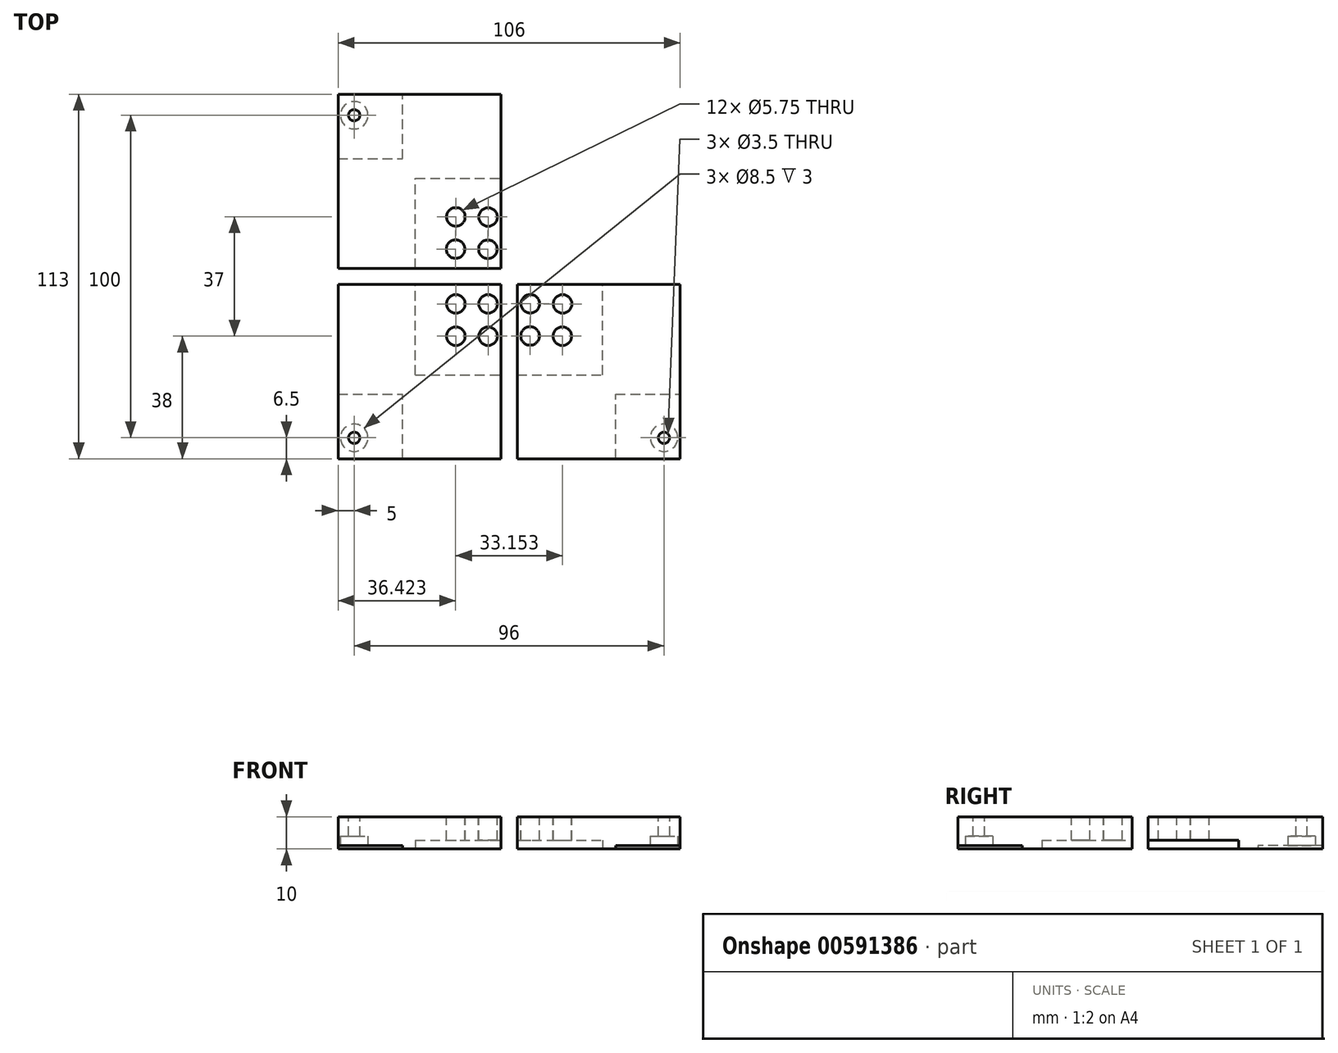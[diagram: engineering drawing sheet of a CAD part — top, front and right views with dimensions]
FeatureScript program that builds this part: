
annotation { "Feature Type Name" : "Feature", "Feature Type Description" : "" }
export const myFeature = defineFeature(function(context is Context, id is Id, definition is map)
    precondition{}
    {
        {
            var Q0;
            Q0=qCreatedBy(makeId("Top.planeOp"),FACE);
            var sketch = newSketch(context, id + "F0", { "sketchPlane" : qUnion([Q0])});
            skLineSegment(sketch, "E0.bottom", {"start": v(-53, 56.5) * mm, "end": v(-2.5, 56.5) * mm});
            skLineSegment(sketch, "E0.top", {"start": v(-53, 2.5) * mm, "end": v(-2.5, 2.5) * mm});
            skLineSegment(sketch, "E0.left", {"start": v(-53, 56.5) * mm, "end": v(-53, 2.5) * mm});
            skLineSegment(sketch, "E0.right", {"start": v(-2.5, 56.5) * mm, "end": v(-2.5, 2.5) * mm});
            skLineSegment(sketch, "E1.bottom", {"start": v(2.5, -2.5) * mm, "end": v(53, -2.5) * mm});
            skLineSegment(sketch, "E1.top", {"start": v(2.5, -56.5) * mm, "end": v(53, -56.5) * mm});
            skLineSegment(sketch, "E1.left", {"start": v(2.5, -2.5) * mm, "end": v(2.5, -56.5) * mm});
            skLineSegment(sketch, "E1.right", {"start": v(53, -2.5) * mm, "end": v(53, -56.5) * mm});
            skLineSegment(sketch, "E2.bottom", {"start": v(-53, -2.5) * mm, "end": v(-2.5, -2.5) * mm});
            skLineSegment(sketch, "E2.top", {"start": v(-53, -56.5) * mm, "end": v(-2.5, -56.5) * mm});
            skLineSegment(sketch, "E2.left", {"start": v(-53, -2.5) * mm, "end": v(-53, -56.5) * mm});
            skLineSegment(sketch, "E2.right", {"start": v(-2.5, -2.5) * mm, "end": v(-2.5, -56.5) * mm});
            skSolve(sketch);
        }
        {
            var Q0;
            Q0=makeQuery(id+"F0.imprint","IMPRINT",FACE,{"disambiguationData":[TD([[makeQuery(id+"F0.imprint","IMPRINT",EDGE,{"derivedFrom":sQuery(id+"F0.wireOp",EDGE,"E0.bottom")}),-1.0]])]});
            var Q1;
            Q1=makeQuery(id+"F0.imprint","IMPRINT",FACE,{"disambiguationData":[TD([[makeQuery(id+"F0.imprint","IMPRINT",EDGE,{"derivedFrom":sQuery(id+"F0.wireOp",EDGE,"E2.bottom")}),-1.0]])]});
            var Q2;
            Q2=makeQuery(id+"F0.imprint","IMPRINT",FACE,{"disambiguationData":[TD([[makeQuery(id+"F0.imprint","IMPRINT",EDGE,{"derivedFrom":sQuery(id+"F0.wireOp",EDGE,"E1.bottom")}),-1.0]])]});
            extrude(context, id + "F1", {"entities" : qUnion([Q0, Q1, Q2]), "endBound" : BoundingType.SYMMETRIC, "depth" : 10 * mm, "offsetDistance" : 25 * mm});
        }
        {
            var Q0;
            Q0=makeQuery(id+"F1.opExtrude","CAP_FACE",FACE,{"disambiguationData":[OSD([sQuery(id+"F0.wireOp",EDGE,"E1.bottom"),sQuery(id+"F0.wireOp",EDGE,"E1.top"),sQuery(id+"F0.wireOp",EDGE,"E1.left"),sQuery(id+"F0.wireOp",EDGE,"E1.right")])],"isStart":false});
            var sketch = newSketch(context, id + "F2", { "sketchPlane" : qUnion([Q0])});
            skCircle(sketch, "E3", {"center": v(48, -50) * mm, "radius": 1.75 * mm});
            skCircle(sketch, "E4", {"center": v(-48, -50) * mm, "radius": 1.75 * mm});
            skCircle(sketch, "E5", {"center": v(-48, 50) * mm, "radius": 1.75 * mm});
            skSolve(sketch);
        }
        {
            var Q0;
            Q0=makeQuery(id+"F2.imprint","IMPRINT",FACE,{"disambiguationData":[TD([[makeQuery(id+"F2.imprint","IMPRINT",EDGE,{"derivedFrom":sQuery(id+"F2.wireOp",EDGE,"E5")}),1.0]])]});
            var Q1;
            Q1=makeQuery(id+"F2.imprint","IMPRINT",FACE,{"disambiguationData":[TD([[makeQuery(id+"F2.imprint","IMPRINT",EDGE,{"derivedFrom":sQuery(id+"F2.wireOp",EDGE,"E4")}),1.0]])]});
            var Q2;
            Q2=makeQuery(id+"F2.imprint","IMPRINT",FACE,{"disambiguationData":[TD([[makeQuery(id+"F2.imprint","IMPRINT",EDGE,{"derivedFrom":sQuery(id+"F2.wireOp",EDGE,"E3")}),1.0]])]});
            var Q3;
            Q3=sQuery(id+"F2.wireOp",EDGE,"E3");
            var Q4;
            Q4=sQuery(id+"F2.wireOp",EDGE,"E4");
            var Q5;
            Q5=sQuery(id+"F2.wireOp",EDGE,"E5");
            extrude(context, id + "F3", {"entities" : qUnion([Q0, Q1, Q2]), "operationType" : NewBodyOperationType.REMOVE, "surfaceEntities" : qUnion([Q3, Q4, Q5]), "oppositeDirection" : true, "depth" : 10 * mm, "offsetDistance" : 25 * mm});
        }
        {
            var Q0;
            Q0=makeQuery(id+"F1.opExtrude","CAP_FACE",FACE,{"disambiguationData":[OSD([sQuery(id+"F0.wireOp",EDGE,"E1.bottom"),sQuery(id+"F0.wireOp",EDGE,"E1.top"),sQuery(id+"F0.wireOp",EDGE,"E1.left"),sQuery(id+"F0.wireOp",EDGE,"E1.right")])],"isStart":false});
            var sketch = newSketch(context, id + "F4", { "sketchPlane" : qUnion([Q0])});
            skCircle(sketch, "E6", {"center": v(16.5, -18.5) * mm, "radius": 2.88 * mm});
            skCircle(sketch, "E7", {"center": v(-16.5, -18.5) * mm, "radius": 2.88 * mm});
            skCircle(sketch, "E8.0.1.0", {"center": v(-16.5, -8.5) * mm, "radius": 2.88 * mm});
            skCircle(sketch, "E8.1.0.0", {"center": v(-6.5, -18.5) * mm, "radius": 2.88 * mm});
            skCircle(sketch, "E8.1.1.0", {"center": v(-6.5, -8.5) * mm, "radius": 2.88 * mm});
            skLineSegment(sketch, "E8.direction1", {"start": v(-16.5, -18.5) * mm, "end": v(-6.5, -18.5) * mm, "construction": true});
            skLineSegment(sketch, "E8.direction2", {"start": v(-16.5, -18.5) * mm, "end": v(-16.5, -8.5) * mm, "construction": true});
            skCircle(sketch, "E9.0.1.0", {"center": v(6.5, -18.45) * mm, "radius": 2.88 * mm});
            skCircle(sketch, "E9.1.0.0", {"center": v(16.58, -8.5) * mm, "radius": 2.88 * mm});
            skCircle(sketch, "E9.1.1.0", {"center": v(6.58, -8.45) * mm, "radius": 2.88 * mm});
            skLineSegment(sketch, "E9.direction1", {"start": v(16.5, -18.5) * mm, "end": v(16.58, -8.5) * mm, "construction": true});
            skLineSegment(sketch, "E9.direction2", {"start": v(16.5, -18.5) * mm, "end": v(6.5, -18.45) * mm, "construction": true});
            skCircle(sketch, "E10", {"center": v(-16.5, 18.5) * mm, "radius": 2.88 * mm});
            skCircle(sketch, "E11.0.1.0", {"center": v(-6.5, 18.45) * mm, "radius": 2.88 * mm});
            skCircle(sketch, "E11.1.0.0", {"center": v(-16.58, 8.5) * mm, "radius": 2.88 * mm});
            skCircle(sketch, "E11.1.1.0", {"center": v(-6.58, 8.45) * mm, "radius": 2.88 * mm});
            skLineSegment(sketch, "E11.direction1", {"start": v(-16.5, 18.5) * mm, "end": v(-16.58, 8.5) * mm, "construction": true});
            skLineSegment(sketch, "E11.direction2", {"start": v(-16.5, 18.5) * mm, "end": v(-6.5, 18.45) * mm, "construction": true});
            skSolve(sketch);
        }
        {
            var Q0;
            Q0=makeQuery(id+"F4.imprint","IMPRINT",FACE,{"disambiguationData":[TD([[makeQuery(id+"F4.imprint","IMPRINT",EDGE,{"derivedFrom":sQuery(id+"F4.wireOp",EDGE,"E11.0.1.0")}),1.0]])]});
            var Q1;
            Q1=makeQuery(id+"F4.imprint","IMPRINT",FACE,{"disambiguationData":[TD([[makeQuery(id+"F4.imprint","IMPRINT",EDGE,{"derivedFrom":sQuery(id+"F4.wireOp",EDGE,"E10")}),1.0]])]});
            var Q2;
            Q2=makeQuery(id+"F4.imprint","IMPRINT",FACE,{"disambiguationData":[TD([[makeQuery(id+"F4.imprint","IMPRINT",EDGE,{"derivedFrom":sQuery(id+"F4.wireOp",EDGE,"E11.1.0.0")}),1.0]])]});
            var Q3;
            Q3=makeQuery(id+"F4.imprint","IMPRINT",FACE,{"disambiguationData":[TD([[makeQuery(id+"F4.imprint","IMPRINT",EDGE,{"derivedFrom":sQuery(id+"F4.wireOp",EDGE,"E11.1.1.0")}),1.0]])]});
            var Q4;
            Q4=makeQuery(id+"F4.imprint","IMPRINT",FACE,{"disambiguationData":[TD([[makeQuery(id+"F4.imprint","IMPRINT",EDGE,{"derivedFrom":sQuery(id+"F4.wireOp",EDGE,"E8.1.1.0")}),1.0]])]});
            var Q5;
            Q5=makeQuery(id+"F4.imprint","IMPRINT",FACE,{"disambiguationData":[TD([[makeQuery(id+"F4.imprint","IMPRINT",EDGE,{"derivedFrom":sQuery(id+"F4.wireOp",EDGE,"E8.0.1.0")}),1.0]])]});
            var Q6;
            Q6=makeQuery(id+"F4.imprint","IMPRINT",FACE,{"disambiguationData":[TD([[makeQuery(id+"F4.imprint","IMPRINT",EDGE,{"derivedFrom":sQuery(id+"F4.wireOp",EDGE,"E7")}),1.0]])]});
            var Q7;
            Q7=makeQuery(id+"F4.imprint","IMPRINT",FACE,{"disambiguationData":[TD([[makeQuery(id+"F4.imprint","IMPRINT",EDGE,{"derivedFrom":sQuery(id+"F4.wireOp",EDGE,"E8.1.0.0")}),1.0]])]});
            var Q8;
            Q8=makeQuery(id+"F4.imprint","IMPRINT",FACE,{"disambiguationData":[TD([[makeQuery(id+"F4.imprint","IMPRINT",EDGE,{"derivedFrom":sQuery(id+"F4.wireOp",EDGE,"E9.0.1.0")}),1.0]])]});
            var Q9;
            Q9=makeQuery(id+"F4.imprint","IMPRINT",FACE,{"disambiguationData":[TD([[makeQuery(id+"F4.imprint","IMPRINT",EDGE,{"derivedFrom":sQuery(id+"F4.wireOp",EDGE,"E9.1.1.0")}),1.0]])]});
            var Q10;
            Q10=makeQuery(id+"F4.imprint","IMPRINT",FACE,{"disambiguationData":[TD([[makeQuery(id+"F4.imprint","IMPRINT",EDGE,{"derivedFrom":sQuery(id+"F4.wireOp",EDGE,"E9.1.0.0")}),1.0]])]});
            var Q11;
            Q11=makeQuery(id+"F4.imprint","IMPRINT",FACE,{"disambiguationData":[TD([[makeQuery(id+"F4.imprint","IMPRINT",EDGE,{"derivedFrom":sQuery(id+"F4.wireOp",EDGE,"E6")}),1.0]])]});
            var Q12;
            Q12=sQuery(id+"F4.wireOp",EDGE,"E10");
            var Q13;
            Q13=sQuery(id+"F4.wireOp",EDGE,"E11.0.1.0");
            var Q14;
            Q14=sQuery(id+"F4.wireOp",EDGE,"E11.1.1.0");
            var Q15;
            Q15=sQuery(id+"F4.wireOp",EDGE,"E11.1.0.0");
            var Q16;
            Q16=sQuery(id+"F4.wireOp",EDGE,"E8.0.1.0");
            var Q17;
            Q17=sQuery(id+"F4.wireOp",EDGE,"E8.1.1.0");
            var Q18;
            Q18=sQuery(id+"F4.wireOp",EDGE,"E8.1.0.0");
            var Q19;
            Q19=sQuery(id+"F4.wireOp",EDGE,"E7");
            var Q20;
            Q20=sQuery(id+"F4.wireOp",EDGE,"E9.0.1.0");
            var Q21;
            Q21=sQuery(id+"F4.wireOp",EDGE,"E6");
            var Q22;
            Q22=sQuery(id+"F4.wireOp",EDGE,"E9.1.0.0");
            var Q23;
            Q23=sQuery(id+"F4.wireOp",EDGE,"E9.1.1.0");
            extrude(context, id + "F5", {"entities" : qUnion([Q0, Q1, Q2, Q3, Q4, Q5, Q6, Q7, Q8, Q9, Q10, Q11]), "operationType" : NewBodyOperationType.REMOVE, "surfaceEntities" : qUnion([Q12, Q13, Q14, Q15, Q16, Q17, Q18, Q19, Q20, Q21, Q22, Q23]), "oppositeDirection" : true, "depth" : 10 * mm, "offsetDistance" : 25 * mm});
        }
        {
            var Q0;
            Q0=makeQuery(id+"F1.opExtrude","CAP_FACE",FACE,{"disambiguationData":[OSD([sQuery(id+"F0.wireOp",EDGE,"E2.bottom"),sQuery(id+"F0.wireOp",EDGE,"E2.top"),sQuery(id+"F0.wireOp",EDGE,"E2.left"),sQuery(id+"F0.wireOp",EDGE,"E2.right")])],"isStart":true});
            var sketch = newSketch(context, id + "F6", { "sketchPlane" : qUnion([Q0])});
            skLineSegment(sketch, "E12.bottom", {"start": v(-29, 30.5) * mm, "end": v(-2.5, 30.5) * mm});
            skLineSegment(sketch, "E12.top", {"start": v(-29, 2.5) * mm, "end": v(-2.5, 2.5) * mm});
            skLineSegment(sketch, "E12.left", {"start": v(-29, 30.5) * mm, "end": v(-29, 2.5) * mm});
            skLineSegment(sketch, "E12.right", {"start": v(-2.5, 30.5) * mm, "end": v(-2.5, 2.5) * mm});
            skLineSegment(sketch, "E13.bottom", {"start": v(2.5, 30.5) * mm, "end": v(29, 30.5) * mm});
            skLineSegment(sketch, "E13.top", {"start": v(2.5, 2.5) * mm, "end": v(29, 2.5) * mm});
            skLineSegment(sketch, "E13.left", {"start": v(2.5, 30.5) * mm, "end": v(2.5, 2.5) * mm});
            skLineSegment(sketch, "E13.right", {"start": v(29, 30.5) * mm, "end": v(29, 2.5) * mm});
            skLineSegment(sketch, "E14.bottom", {"start": v(-29, -2.5) * mm, "end": v(-2.5, -2.5) * mm});
            skLineSegment(sketch, "E14.top", {"start": v(-29, -30.5) * mm, "end": v(-2.5, -30.5) * mm});
            skLineSegment(sketch, "E14.left", {"start": v(-29, -2.5) * mm, "end": v(-29, -30.5) * mm});
            skLineSegment(sketch, "E14.right", {"start": v(-2.5, -2.5) * mm, "end": v(-2.5, -30.5) * mm});
            skSolve(sketch);
        }
        {
            var Q0;
            Q0=makeQuery(id+"F6.imprint","IMPRINT",FACE,{"disambiguationData":[TD([[makeQuery(id+"F6.imprint","IMPRINT",EDGE,{"derivedFrom":sQuery(id+"F6.wireOp",EDGE,"E13.bottom")}),-1.0]])]});
            var Q1;
            Q1=makeQuery(id+"F6.imprint","IMPRINT",FACE,{"disambiguationData":[TD([[makeQuery(id+"F6.imprint","IMPRINT",EDGE,{"derivedFrom":sQuery(id+"F6.wireOp",EDGE,"E14.bottom")}),-1.0]])]});
            var Q2;
            Q2=makeQuery(id+"F6.imprint","IMPRINT",FACE,{"disambiguationData":[TD([[makeQuery(id+"F6.imprint","IMPRINT",EDGE,{"derivedFrom":sQuery(id+"F6.wireOp",EDGE,"E12.bottom")}),-1.0]])]});
            extrude(context, id + "F7", {"entities" : qUnion([Q0, Q1, Q2]), "operationType" : NewBodyOperationType.REMOVE, "oppositeDirection" : true, "depth" : 2.75 * mm, "offsetDistance" : 25 * mm});
        }
        {
            var Q0;
            Q0=makeQuery(id+"F1.opExtrude","CAP_FACE",FACE,{"disambiguationData":[OSD([sQuery(id+"F0.wireOp",EDGE,"E0.bottom"),sQuery(id+"F0.wireOp",EDGE,"E0.top"),sQuery(id+"F0.wireOp",EDGE,"E0.left"),sQuery(id+"F0.wireOp",EDGE,"E0.right")])],"isStart":true});
            var sketch = newSketch(context, id + "F8", { "sketchPlane" : qUnion([Q0])});
            skLineSegment(sketch, "E15.bottom", {"start": v(-53, -36.5) * mm, "end": v(-33, -36.5) * mm});
            skLineSegment(sketch, "E15.top", {"start": v(-53, -56.5) * mm, "end": v(-33, -56.5) * mm});
            skLineSegment(sketch, "E15.left", {"start": v(-53, -36.5) * mm, "end": v(-53, -56.5) * mm});
            skLineSegment(sketch, "E15.right", {"start": v(-33, -36.5) * mm, "end": v(-33, -56.5) * mm});
            skLineSegment(sketch, "E16.bottom", {"start": v(-53, 56.5) * mm, "end": v(-33, 56.5) * mm});
            skLineSegment(sketch, "E16.top", {"start": v(-53, 36.5) * mm, "end": v(-33, 36.5) * mm});
            skLineSegment(sketch, "E16.left", {"start": v(-53, 56.5) * mm, "end": v(-53, 36.5) * mm});
            skLineSegment(sketch, "E16.right", {"start": v(-33, 56.5) * mm, "end": v(-33, 36.5) * mm});
            skLineSegment(sketch, "E17.bottom", {"start": v(33, 56.5) * mm, "end": v(53, 56.5) * mm});
            skLineSegment(sketch, "E17.top", {"start": v(33, 36.5) * mm, "end": v(53, 36.5) * mm});
            skLineSegment(sketch, "E17.left", {"start": v(33, 56.5) * mm, "end": v(33, 36.5) * mm});
            skLineSegment(sketch, "E17.right", {"start": v(53, 56.5) * mm, "end": v(53, 36.5) * mm});
            skSolve(sketch);
        }
        {
            var Q0;
            Q0=makeQuery(id+"F8.imprint","IMPRINT",FACE,{"disambiguationData":[TD([[makeQuery(id+"F8.imprint","IMPRINT",EDGE,{"derivedFrom":sQuery(id+"F8.wireOp",EDGE,"E15.bottom")}),-1.0]])]});
            var Q1;
            Q1=makeQuery(id+"F8.imprint","IMPRINT",FACE,{"disambiguationData":[TD([[makeQuery(id+"F8.imprint","IMPRINT",EDGE,{"derivedFrom":sQuery(id+"F8.wireOp",EDGE,"E16.bottom")}),-1.0]])]});
            var Q2;
            Q2=makeQuery(id+"F8.imprint","IMPRINT",FACE,{"disambiguationData":[TD([[makeQuery(id+"F8.imprint","IMPRINT",EDGE,{"derivedFrom":sQuery(id+"F8.wireOp",EDGE,"E17.bottom")}),-1.0]])]});
            extrude(context, id + "F9", {"entities" : qUnion([Q0, Q1, Q2]), "operationType" : NewBodyOperationType.REMOVE, "oppositeDirection" : true, "depth" : 1 * mm, "offsetDistance" : 25 * mm});
        }
        {
            var Q0;
            Q0=makeQuery(id+"F9.boolean.opBoolean","COPY",FACE,{"derivedFrom":makeQuery(id+"F9.opExtrude","CAP_FACE",FACE,{"disambiguationData":[OSD([sQuery(id+"F8.wireOp",EDGE,"E16.bottom"),sQuery(id+"F8.wireOp",EDGE,"E16.top"),sQuery(id+"F8.wireOp",EDGE,"E16.left"),sQuery(id+"F8.wireOp",EDGE,"E16.right")])],"isStart":false})});
            var sketch = newSketch(context, id + "F10", { "sketchPlane" : qUnion([Q0])});
            skCircle(sketch, "E18", {"center": v(-48, 50) * mm, "radius": 4.25 * mm});
            skCircle(sketch, "E19", {"center": v(48, 50) * mm, "radius": 4.25 * mm});
            skCircle(sketch, "E20", {"center": v(-48, -50) * mm, "radius": 4.25 * mm});
            skSolve(sketch);
        }
        {
            var Q0;
            {var subQ0=sQuery(id+"F10.wireOp",EDGE,"E18");var subQ1=sQuery(id+"F8.wireOp",EDGE,"E16.bottom");var subQ2=makeQuery(id+"F9.boolean.opBoolean","COPY",EDGE,{"derivedFrom":makeQuery(id+"F9.opExtrude","CAP_EDGE",EDGE,{"disambiguationData":[OSD([subQ1])],"isStart":false})});var subQ3=makeQuery(id+"F10.imprint","INTERSECT",VERTEX,{"derivedFrom":[subQ2,subQ0]});Q0=makeQuery(id+"F10.imprint","IMPRINT",FACE,{"disambiguationData":[TD([[makeQuery(id+"F10.imprint","IMPRINT",EDGE,{"disambiguationData":[TD([[subQ3,1.0]])],"derivedFrom":subQ0}),1.0]])]});}
            var Q1;
            Q1=makeQuery(id+"F10.imprint","IMPRINT",FACE,{"disambiguationData":[TD([[makeQuery(id+"F10.imprint","IMPRINT",EDGE,{"derivedFrom":sQuery(id+"F10.wireOp",EDGE,"E19")}),1.0]])]});
            var Q2;
            Q2=makeQuery(id+"F10.imprint","IMPRINT",FACE,{"disambiguationData":[TD([[makeQuery(id+"F10.imprint","IMPRINT",EDGE,{"derivedFrom":sQuery(id+"F10.wireOp",EDGE,"E20")}),1.0]])]});
            var Q3;
            {var subQ0=sQuery(id+"F10.wireOp",EDGE,"E18");var subQ1=makeQuery(id+"F9.boolean.opBoolean","COPY",EDGE,{"derivedFrom":makeQuery(id+"F9.opExtrude","CAP_EDGE",EDGE,{"disambiguationData":[OSD([sQuery(id+"F8.wireOp",EDGE,"E16.left")])],"isStart":false})});var subQ2=makeQuery(id+"F10.imprint","INTERSECT",VERTEX,{"disambiguationData":[OD(0.0)],"derivedFrom":[subQ1,subQ0]});Q3=makeQuery(id+"F10.imprint","IMPRINT",FACE,{"disambiguationData":[TD([[makeQuery(id+"F10.imprint","IMPRINT",EDGE,{"disambiguationData":[TD([[subQ2,-1.0]])],"derivedFrom":subQ0}),1.0]])]});}
            var Q4;
            {var subQ1=sQuery(id+"F8.wireOp",EDGE,"E16.bottom");var subQ2=sQuery(id+"F10.wireOp",EDGE,"E18");var subQ3=makeQuery(id+"F9.boolean.opBoolean","COPY",EDGE,{"derivedFrom":makeQuery(id+"F9.opExtrude","CAP_EDGE",EDGE,{"disambiguationData":[OSD([subQ1])],"isStart":false})});var subQ8=makeQuery(id+"F10.imprint","INTERSECT",VERTEX,{"disambiguationData":[OD(0.0)],"derivedFrom":[subQ3,subQ2]});Q4=makeQuery(id+"F10.imprint","IMPRINT",FACE,{"disambiguationData":[TD([[makeQuery(id+"F10.imprint","IMPRINT",EDGE,{"disambiguationData":[TD([[subQ8,-1.0]])],"derivedFrom":subQ2}),1.0]])]});}
            extrude(context, id + "F11", {"entities" : qUnion([Q0, Q1, Q2, Q3, Q4]), "operationType" : NewBodyOperationType.REMOVE, "oppositeDirection" : true, "depth" : 3 * mm, "offsetDistance" : 25 * mm});
        }
    });
